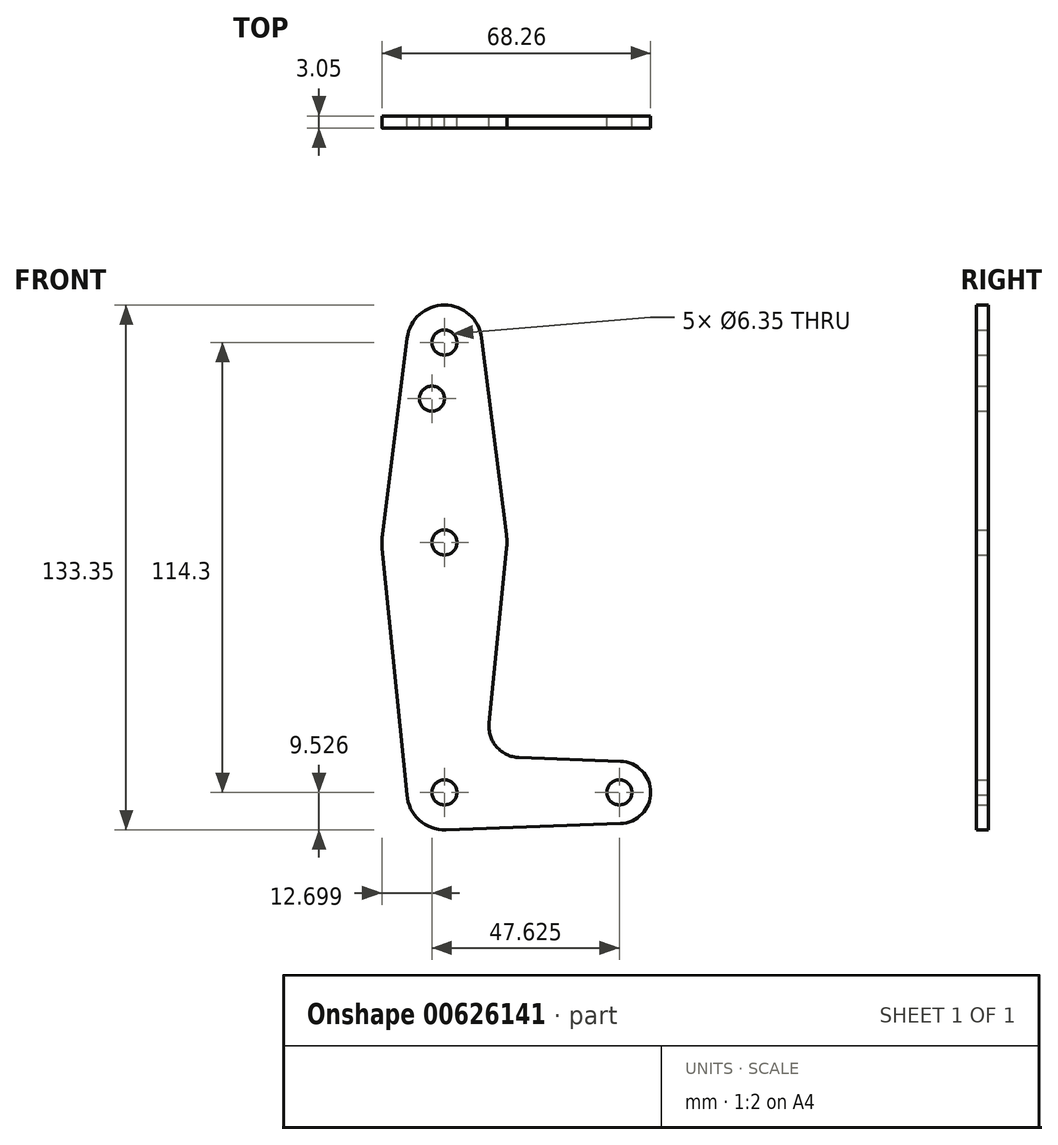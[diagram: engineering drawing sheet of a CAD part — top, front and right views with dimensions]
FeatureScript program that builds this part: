
annotation { "Feature Type Name" : "Feature", "Feature Type Description" : "" }
export const myFeature = defineFeature(function(context is Context, id is Id, definition is map)
    precondition{}
    {
        {
            var Q0;
            Q0=qCreatedBy(makeId("Front.planeOp"),FACE);
            var sketch = newSketch(context, id + "F0", { "sketchPlane" : qUnion([Q0])});
            skLineSegment(sketch, "E0", {"start": v(-539.96, -26.48) * mm, "end": v(-539.96, -89.98) * mm, "construction": true});
            skLineSegment(sketch, "E1", {"start": v(-539.96, -89.98) * mm, "end": v(-495.5, -89.98) * mm, "construction": true});
            skCircle(sketch, "E2", {"center": v(-539.96, -26.48) * mm, "radius": 15.88 * mm});
            skCircle(sketch, "E3", {"center": v(-539.96, -89.98) * mm, "radius": 9.53 * mm});
            skCircle(sketch, "E4", {"center": v(-495.5, -89.98) * mm, "radius": 7.94 * mm});
            skCircle(sketch, "E5", {"center": v(-539.96, 24.32) * mm, "radius": 9.53 * mm});
            skLineSegment(sketch, "E6", {"start": v(-539.96, -26.48) * mm, "end": v(-539.96, 24.32) * mm, "construction": true});
            skLineSegment(sketch, "E7", {"start": v(-555.7, -24.5) * mm, "end": v(-549.4, 25.5) * mm});
            skLineSegment(sketch, "E8", {"start": v(-524.2, -24.5) * mm, "end": v(-530.5, 25.5) * mm});
            skLineSegment(sketch, "E9", {"start": v(-549.46, -90.57) * mm, "end": v(-555.75, -28.07) * mm});
            skLineSegment(sketch, "E10", {"start": v(-524.16, -28.07) * mm, "end": v(-528.61, -72.4) * mm});
            skLineSegment(sketch, "E11", {"start": v(-520.99, -81.13) * mm, "end": v(-495.22, -82.05) * mm});
            skLineSegment(sketch, "E12", {"start": v(-539.62, -99.5) * mm, "end": v(-495.22, -97.92) * mm});
            skCircle(sketch, "E13", {"center": v(-539.96, 24.32) * mm, "radius": 3.18 * mm});
            skCircle(sketch, "E14", {"center": v(-539.96, -26.48) * mm, "radius": 3.18 * mm});
            skCircle(sketch, "E15", {"center": v(-539.96, -89.98) * mm, "radius": 3.18 * mm});
            skCircle(sketch, "E16", {"center": v(-495.5, -89.98) * mm, "radius": 3.18 * mm});
            skCircle(sketch, "E17", {"center": v(-543.13, 10.04) * mm, "radius": 3.18 * mm});
            skArc(sketch, "E18.filletArc", {"start": v(-528.61, -72.4) * mm, "mid": v(-526.7, -78.41) * mm, "end": v(-520.99, -81.13) * mm});
            skSolve(sketch);
        }
        {
            var Q0;
            Q0 = qSketchRegion(id + "F0", true);
            extrude(context, id + "F1", {"entities" : qUnion([Q0]), "depth" : 3.05 * mm, "offsetDistance" : 25.4 * mm});
        }
    });
